FCSTD DOCUMENT  (FreeCAD 0.18R16110 (Git))
Label: 5sideP
License: All rights reserved
LicenseURL: http://en.wikipedia.org/wiki/All_rights_reserved
objects: Sketcher::SketchObject×1
note: 1 computed .brp shape members not serialized (recipe doc carries the construction recipe); baked Part::Feature solids carry a one-line shape summary decoded from their .brp

FEATURE [Sketcher::SketchObject] Sketch
  sketch-geometry (16):
    g0: LineSegment [constr] StartX=-1281.94 StartY=0 StartZ=0 EndX=-396.142 EndY=-1219.2 EndZ=0
    g1: LineSegment [constr] StartX=-396.142 StartY=-1219.2 StartZ=0 EndX=1037.11 EndY=-753.507 EndZ=0
    g2: LineSegment [constr] StartX=1037.11 StartY=-753.507 StartZ=0 EndX=1037.11 EndY=753.507 EndZ=0
    g3: LineSegment [constr] StartX=1037.11 StartY=753.507 StartZ=0 EndX=-396.142 EndY=1219.2 EndZ=0
    g4: LineSegment [constr] StartX=-396.142 StartY=1219.2 StartZ=0 EndX=-1281.94 EndY=0 EndZ=0
    g5: Circle [constr] CenterX=0 CenterY=0 CenterZ=0 NormalX=0 NormalY=0 NormalZ=1 AngleXU=0 Radius=1281.94
    g6: Circle [constr] CenterX=0 CenterY=0 CenterZ=0 NormalX=0 NormalY=0 NormalZ=1 AngleXU=0 Radius=250
    g7: LineSegment [constr] StartX=-1281.94 StartY=0 StartZ=0 EndX=-229.947 EndY=98.1032 EndZ=0
    g8: LineSegment [constr] StartX=-396.142 StartY=1219.2 StartZ=0 EndX=8.7721 EndY=249.846 EndZ=0
    g9: LineSegment [constr] StartX=1037.11 StartY=753.507 StartZ=0 EndX=243.134 EndY=58.1871 EndZ=0
    g10: LineSegment [constr] StartX=1037.11 StartY=-753.507 StartZ=0 EndX=113.675 EndY=-222.661 EndZ=0
    g11: LineSegment [constr] StartX=-396.142 StartY=-1219.2 StartZ=0 EndX=-185.935 EndY=-167.117 EndZ=0
    g12: LineSegment [constr] StartX=-396.142 StartY=1219.2 StartZ=0 EndX=-396.142 EndY=-1219.2 EndZ=0
    g13: LineSegment [constr] StartX=0 StartY=0 StartZ=0 EndX=-136.449 EndY=-209.48 EndZ=0
    g14: LineSegment [constr] StartX=0 StartY=0 StartZ=0 EndX=-113.191 EndY=222.908 EndZ=0
    g15: LineSegment [constr] StartX=0 StartY=0 StartZ=0 EndX=249.639 EndY=-13.4281 EndZ=0
  constraints (36):
    c: Coincident(g0,g1)
    c: Coincident(g1,g2)
    c: Coincident(g2,g3)
    c: Coincident(g3,g4)
    c: Coincident(g4,g0)
    c: Equal(g0, g1-g4) x4
    c: PointOnObject(g0,g5)
    c: PointOnObject(g1,g5)
    c: PointOnObject(g2,g5)
    c: PointOnObject(g3,g5)
    c: PointOnObject(g4,g5)
    c: Coincident(g5,g-1)
    c: PointOnObject(g4,g-1)
    c: PointOnObject(g8,g6)
    c: PointOnObject(g7,g6)
    c: Coincident(g6,g-1)
    c: Coincident(g7,g0)
    c: Coincident(g8,g3)
    c: Coincident(g9,g2)
    c: Coincident(g10,g1)
    c: Coincident(g11,g0)
    c: Coincident(g12,g3)
    c: Coincident(g12,g0)
    c: Distance(g12) = 2438.4
    c: PointOnObject(g11,g6)
    c: PointOnObject(g9,g6)
    c: PointOnObject(g10,g6)
    c: Radius(g6) = 250
    c: Coincident(g13,g-1)
    c: Coincident(g14,g-1)
    c: Coincident(g15,g-1)
    c: Angle(g13,g15) = 2.0944
    c: Angle(g14,g13) = 2.0944
    c: Equal(g14,g15)
    c: Equal(g15,g13)
    c: Distance(g13) = 250
